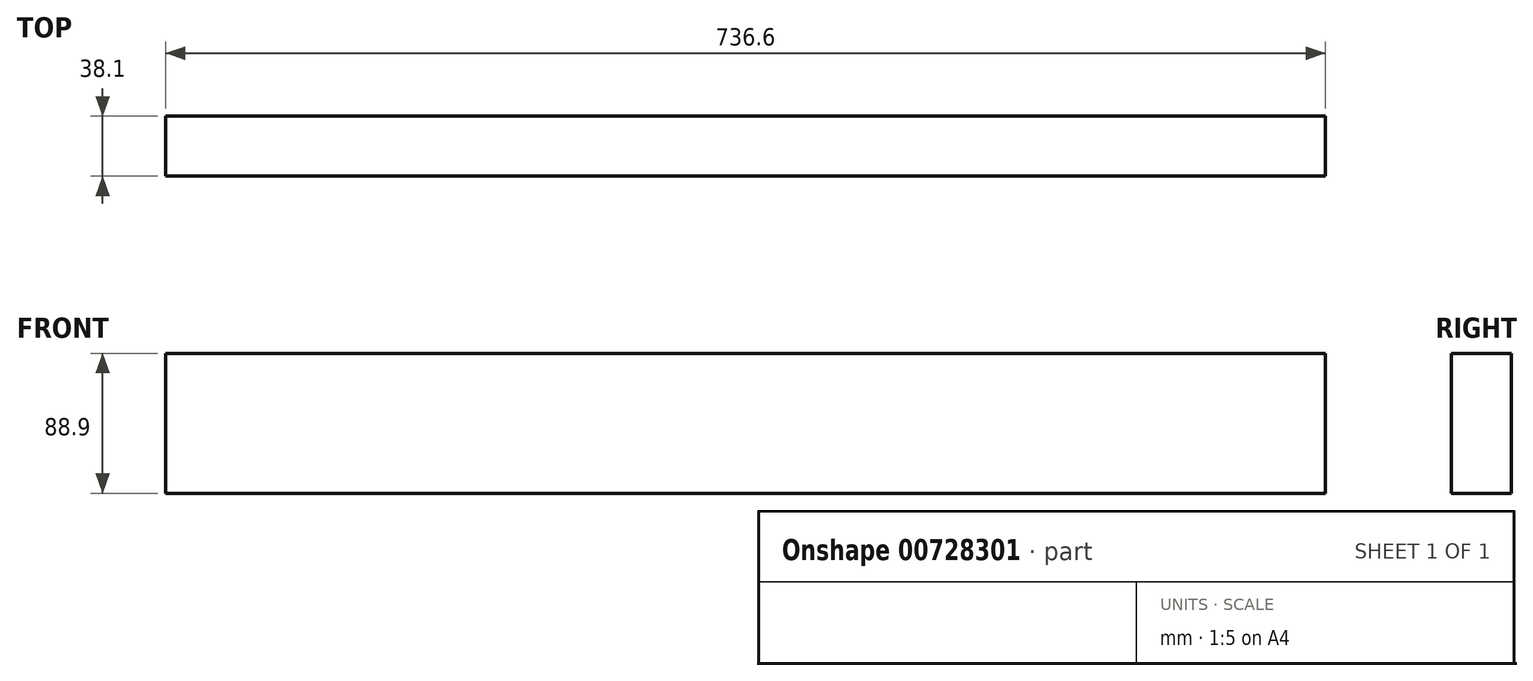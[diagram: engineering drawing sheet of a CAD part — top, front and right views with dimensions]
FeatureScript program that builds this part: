
annotation { "Feature Type Name" : "Feature", "Feature Type Description" : "" }
export const myFeature = defineFeature(function(context is Context, id is Id, definition is map)
    precondition{}
    {
        {
            var Q0;
            Q0=qCreatedBy(makeId("Front.planeOp"),FACE);
            var sketch = newSketch(context, id + "F0", { "sketchPlane" : qUnion([Q0])});
            skLineSegment(sketch, "E0.bottom", {"start": v(-368.3, -44.45) * mm, "end": v(368.3, -44.45) * mm});
            skLineSegment(sketch, "E0.top", {"start": v(-368.3, 44.45) * mm, "end": v(368.3, 44.45) * mm});
            skLineSegment(sketch, "E0.left", {"start": v(-368.3, -44.45) * mm, "end": v(-368.3, 44.45) * mm});
            skLineSegment(sketch, "E0.right", {"start": v(368.3, -44.45) * mm, "end": v(368.3, 44.45) * mm});
            skPoint(sketch, "E0.middle", {"position": v(0, 0) * mm});
            skSolve(sketch);
        }
        {
            var Q0;
            Q0=qSketchRegion(id+"F0",true);
            extrude(context, id + "F1", {"entities" : qUnion([Q0]), "depth" : 38.1 * mm, "offsetDistance" : 25.4 * mm});
        }
    });
